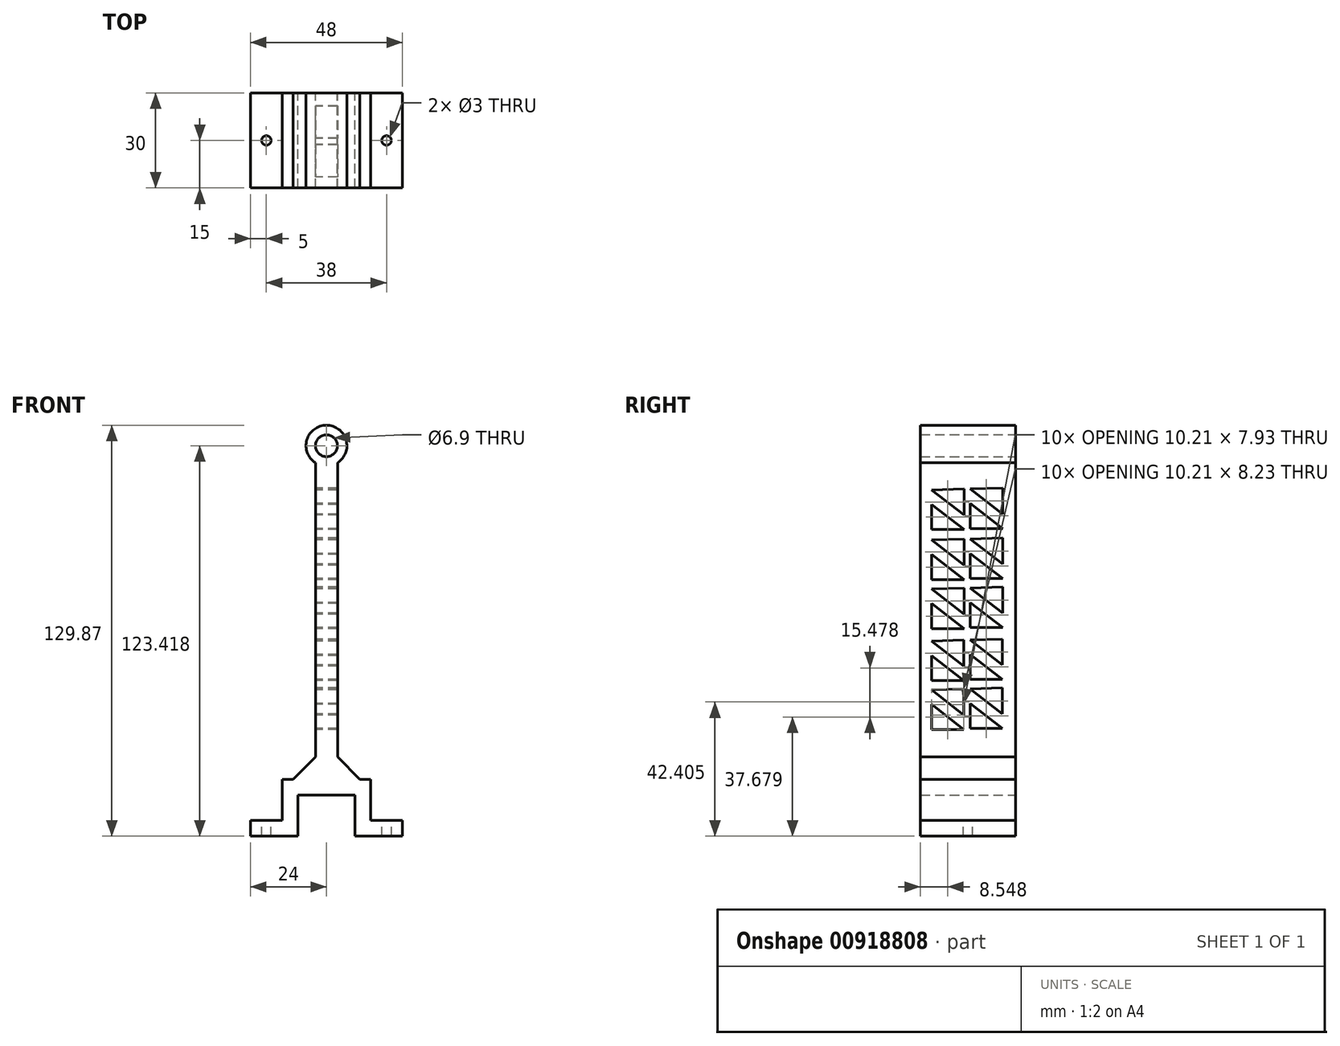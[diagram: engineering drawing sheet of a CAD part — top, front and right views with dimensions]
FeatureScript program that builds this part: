
annotation { "Feature Type Name" : "Feature", "Feature Type Description" : "" }
export const myFeature = defineFeature(function(context is Context, id is Id, definition is map)
    precondition{}
    {
        {
            var Q0;
            Q0=qCreatedBy(makeId("Front.planeOp"),FACE);
            var sketch = newSketch(context, id + "F0", { "sketchPlane" : qUnion([Q0])});
            skLineSegment(sketch, "E0", {"start": v(-24, 0) * mm, "end": v(-9, 0) * mm});
            skLineSegment(sketch, "E1", {"start": v(-9, 0) * mm, "end": v(-9, 13) * mm});
            skLineSegment(sketch, "E2", {"start": v(-9, 13) * mm, "end": v(0, 13) * mm});
            skLineSegment(sketch, "E3", {"start": v(-24, 0) * mm, "end": v(-24, 5) * mm});
            skLineSegment(sketch, "E4", {"start": v(-24, 5) * mm, "end": v(-14, 5) * mm});
            skLineSegment(sketch, "E5", {"start": v(-14, 5) * mm, "end": v(-14, 18) * mm});
            skLineSegment(sketch, "E6", {"start": v(-14, 18) * mm, "end": v(0, 18) * mm});
            skLineSegment(sketch, "E7.MirrorCS", {"start": v(14, 18) * mm, "end": v(0, 18) * mm});
            skLineSegment(sketch, "E8.MirrorCS", {"start": v(9, 13) * mm, "end": v(0, 13) * mm});
            skLineSegment(sketch, "E9.MirrorCS", {"start": v(14, 5) * mm, "end": v(14, 18) * mm});
            skLineSegment(sketch, "E10.MirrorCS", {"start": v(9, 0) * mm, "end": v(9, 13) * mm});
            skLineSegment(sketch, "E11.MirrorCS", {"start": v(24, 0) * mm, "end": v(9, 0) * mm});
            skLineSegment(sketch, "E12.MirrorCS", {"start": v(24, 5) * mm, "end": v(14, 5) * mm});
            skLineSegment(sketch, "E13.MirrorCS", {"start": v(24, 0) * mm, "end": v(24, 5) * mm});
            skLineSegment(sketch, "E14", {"start": v(-3.5, 118) * mm, "end": v(-3.5, 18) * mm});
            skLineSegment(sketch, "E15.MirrorCS", {"start": v(3.5, 118) * mm, "end": v(3.5, 18) * mm});
            skCircle(sketch, "E16", {"center": v(0, 123.42) * mm, "radius": 6.45 * mm});
            skCircle(sketch, "E17", {"center": v(0, 123.42) * mm, "radius": 3.45 * mm});
            skLineSegment(sketch, "E18", {"start": v(-3.5, 25.07) * mm, "end": v(-10.57, 18) * mm});
            skLineSegment(sketch, "E19.MirrorCS", {"start": v(3.5, 25.07) * mm, "end": v(10.57, 18) * mm});
            skSolve(sketch);
        }
        {
            var Q0;
            Q0 = qSketchRegion(id + "F0", true);
            extrude(context, id + "F1", {"entities" : qUnion([Q0]), "depth" : 30 * mm, "offsetDistance" : 25.4 * mm});
        }
        {
            var Q0;
            Q0=makeQuery(id+"F1.opExtrude","SWEPT_FACE",FACE,{"disambiguationData":[OSD([sQuery(id+"F0.wireOp",EDGE,"E12.MirrorCS")])]});
            var sketch = newSketch(context, id + "F2", { "sketchPlane" : qUnion([Q0])});
            skCircle(sketch, "E20", {"center": v(19, -15) * mm, "radius": 1.5 * mm});
            skCircle(sketch, "E21.MirrorC", {"center": v(-19, -15) * mm, "radius": 1.5 * mm});
            skSolve(sketch);
        }
        {
            var Q0;
            Q0 = qSketchRegion(id + "F2", true);
            extrude(context, id + "F3", {"entities" : qUnion([Q0]), "operationType" : NewBodyOperationType.REMOVE, "oppositeDirection" : true, "depth" : 25.4 * mm, "offsetDistance" : 25.4 * mm});
        }
        {
            var Q0;
            Q0=makeQuery(id+"F1.opExtrude","SWEPT_FACE",FACE,{"disambiguationData":[OSD([sQuery(id+"F0.wireOp",EDGE,"E14")])]});
            var sketch = newSketch(context, id + "F4", { "sketchPlane" : qUnion([Q0])});
            skLineSegment(sketch, "E22", {"start": v(4.14, 34.05) * mm, "end": v(14.35, 34.05) * mm});
            skLineSegment(sketch, "E23", {"start": v(14.35, 34.05) * mm, "end": v(14.35, 41.97) * mm});
            skLineSegment(sketch, "E24", {"start": v(14.35, 41.97) * mm, "end": v(4.14, 34.05) * mm});
            skLineSegment(sketch, "E25", {"start": v(14.35, 46.55) * mm, "end": v(4.14, 38.62) * mm});
            skLineSegment(sketch, "E26", {"start": v(4.14, 38.62) * mm, "end": v(4.14, 46.85) * mm});
            skLineSegment(sketch, "E27", {"start": v(4.14, 46.85) * mm, "end": v(14.35, 46.55) * mm});
            skLineSegment(sketch, "E28", {"start": v(4.14, 49.53) * mm, "end": v(14.35, 49.53) * mm});
            skLineSegment(sketch, "E29", {"start": v(14.35, 49.53) * mm, "end": v(14.35, 57.45) * mm});
            skLineSegment(sketch, "E30", {"start": v(14.35, 57.45) * mm, "end": v(4.14, 49.53) * mm});
            skLineSegment(sketch, "E31", {"start": v(14.35, 62.02) * mm, "end": v(4.14, 54.1) * mm});
            skLineSegment(sketch, "E32", {"start": v(4.14, 54.1) * mm, "end": v(4.14, 62.33) * mm});
            skLineSegment(sketch, "E33", {"start": v(4.14, 62.33) * mm, "end": v(14.35, 62.02) * mm});
            skLineSegment(sketch, "E34", {"start": v(4.07, 65.95) * mm, "end": v(14.28, 65.95) * mm});
            skLineSegment(sketch, "E35", {"start": v(14.28, 65.95) * mm, "end": v(14.28, 73.87) * mm});
            skLineSegment(sketch, "E36", {"start": v(14.28, 73.87) * mm, "end": v(4.07, 65.95) * mm});
            skLineSegment(sketch, "E37", {"start": v(14.28, 78.45) * mm, "end": v(4.07, 70.52) * mm});
            skLineSegment(sketch, "E38", {"start": v(4.07, 70.52) * mm, "end": v(4.07, 78.75) * mm});
            skLineSegment(sketch, "E39", {"start": v(4.07, 78.75) * mm, "end": v(14.28, 78.45) * mm});
            skLineSegment(sketch, "E40", {"start": v(4.07, 81.43) * mm, "end": v(14.28, 81.43) * mm});
            skLineSegment(sketch, "E41", {"start": v(14.28, 81.43) * mm, "end": v(14.28, 89.35) * mm});
            skLineSegment(sketch, "E42", {"start": v(14.28, 89.35) * mm, "end": v(4.07, 81.43) * mm});
            skLineSegment(sketch, "E43", {"start": v(14.28, 93.93) * mm, "end": v(4.07, 86) * mm});
            skLineSegment(sketch, "E44", {"start": v(4.07, 86) * mm, "end": v(4.07, 94.23) * mm});
            skLineSegment(sketch, "E45", {"start": v(4.07, 94.23) * mm, "end": v(14.28, 93.93) * mm});
            skLineSegment(sketch, "E46", {"start": v(16.35, 33.72) * mm, "end": v(26.56, 33.72) * mm});
            skLineSegment(sketch, "E47", {"start": v(26.56, 33.72) * mm, "end": v(26.56, 41.64) * mm});
            skLineSegment(sketch, "E48", {"start": v(26.56, 41.64) * mm, "end": v(16.35, 33.72) * mm});
            skLineSegment(sketch, "E49", {"start": v(26.56, 46.22) * mm, "end": v(16.35, 38.29) * mm});
            skLineSegment(sketch, "E50", {"start": v(16.35, 38.29) * mm, "end": v(16.35, 46.52) * mm});
            skLineSegment(sketch, "E51", {"start": v(16.35, 46.52) * mm, "end": v(26.56, 46.22) * mm});
            skLineSegment(sketch, "E52", {"start": v(16.35, 49.2) * mm, "end": v(26.56, 49.2) * mm});
            skLineSegment(sketch, "E53", {"start": v(26.56, 49.2) * mm, "end": v(26.56, 57.12) * mm});
            skLineSegment(sketch, "E54", {"start": v(26.56, 57.12) * mm, "end": v(16.35, 49.2) * mm});
            skLineSegment(sketch, "E55", {"start": v(26.56, 61.7) * mm, "end": v(16.35, 53.77) * mm});
            skLineSegment(sketch, "E56", {"start": v(16.35, 53.77) * mm, "end": v(16.35, 62) * mm});
            skLineSegment(sketch, "E57", {"start": v(16.35, 62) * mm, "end": v(26.56, 61.7) * mm});
            skLineSegment(sketch, "E58", {"start": v(16.27, 65.62) * mm, "end": v(26.49, 65.62) * mm});
            skLineSegment(sketch, "E59", {"start": v(26.49, 65.62) * mm, "end": v(26.49, 73.54) * mm});
            skLineSegment(sketch, "E60", {"start": v(26.49, 73.54) * mm, "end": v(16.27, 65.62) * mm});
            skLineSegment(sketch, "E61", {"start": v(26.49, 78.12) * mm, "end": v(16.27, 70.19) * mm});
            skLineSegment(sketch, "E62", {"start": v(16.27, 70.19) * mm, "end": v(16.27, 78.42) * mm});
            skLineSegment(sketch, "E63", {"start": v(16.27, 78.42) * mm, "end": v(26.49, 78.12) * mm});
            skLineSegment(sketch, "E64", {"start": v(16.27, 81.1) * mm, "end": v(26.49, 81.1) * mm});
            skLineSegment(sketch, "E65", {"start": v(26.49, 81.1) * mm, "end": v(26.49, 89.02) * mm});
            skLineSegment(sketch, "E66", {"start": v(26.49, 89.02) * mm, "end": v(16.27, 81.1) * mm});
            skLineSegment(sketch, "E67", {"start": v(26.49, 93.6) * mm, "end": v(16.27, 85.67) * mm});
            skLineSegment(sketch, "E68", {"start": v(16.27, 85.67) * mm, "end": v(16.27, 93.9) * mm});
            skLineSegment(sketch, "E69", {"start": v(16.27, 93.9) * mm, "end": v(26.49, 93.6) * mm});
            skLineSegment(sketch, "E70", {"start": v(4.07, 97.25) * mm, "end": v(14.28, 97.25) * mm});
            skLineSegment(sketch, "E71", {"start": v(14.28, 97.25) * mm, "end": v(14.28, 105.18) * mm});
            skLineSegment(sketch, "E72", {"start": v(14.28, 105.18) * mm, "end": v(4.07, 97.25) * mm});
            skLineSegment(sketch, "E73", {"start": v(14.28, 109.75) * mm, "end": v(4.07, 101.83) * mm});
            skLineSegment(sketch, "E74", {"start": v(4.07, 101.83) * mm, "end": v(4.07, 110.06) * mm});
            skLineSegment(sketch, "E75", {"start": v(4.07, 110.06) * mm, "end": v(14.28, 109.75) * mm});
            skLineSegment(sketch, "E76", {"start": v(16.27, 96.92) * mm, "end": v(26.49, 96.92) * mm});
            skLineSegment(sketch, "E77", {"start": v(26.49, 96.92) * mm, "end": v(26.49, 104.85) * mm});
            skLineSegment(sketch, "E78", {"start": v(26.49, 104.85) * mm, "end": v(16.27, 96.92) * mm});
            skLineSegment(sketch, "E79", {"start": v(26.49, 109.42) * mm, "end": v(16.27, 101.5) * mm});
            skLineSegment(sketch, "E80", {"start": v(16.27, 101.5) * mm, "end": v(16.27, 109.72) * mm});
            skLineSegment(sketch, "E81", {"start": v(16.27, 109.72) * mm, "end": v(26.49, 109.42) * mm});
            skSolve(sketch);
        }
        {
            var Q0;
            Q0 = qSketchRegion(id + "F4", true);
            extrude(context, id + "F5", {"entities" : qUnion([Q0]), "operationType" : NewBodyOperationType.REMOVE, "oppositeDirection" : true, "depth" : 25.4 * mm, "offsetDistance" : 25.4 * mm});
        }
    });
